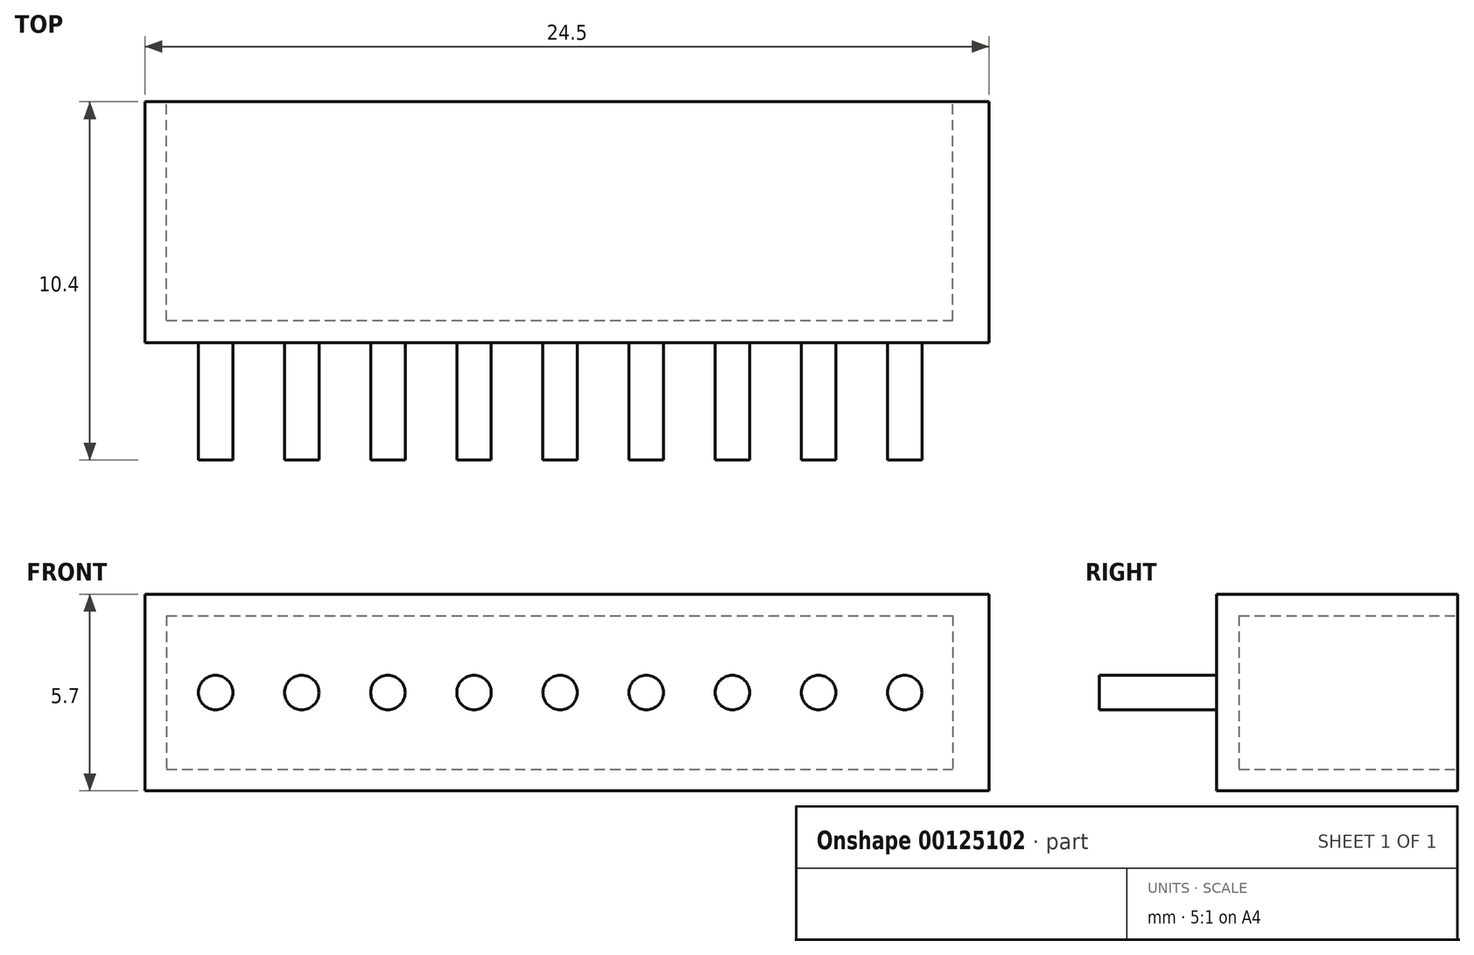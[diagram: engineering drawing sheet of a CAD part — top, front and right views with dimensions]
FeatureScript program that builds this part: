
annotation { "Feature Type Name" : "Feature", "Feature Type Description" : "" }
export const myFeature = defineFeature(function(context is Context, id is Id, definition is map)
    precondition{}
    {
        {
            var Q0;
            Q0=qCreatedBy(makeId("Front.planeOp"),FACE);
            var sketch = newSketch(context, id + "F0", { "sketchPlane" : qUnion([Q0])});
            skLineSegment(sketch, "E0.bottom", {"start": v(12.25, 2.85) * mm, "end": v(-12.25, 2.85) * mm});
            skLineSegment(sketch, "E0.top", {"start": v(12.25, -2.85) * mm, "end": v(-12.25, -2.85) * mm});
            skLineSegment(sketch, "E0.left", {"start": v(12.25, 2.85) * mm, "end": v(12.25, -2.85) * mm});
            skLineSegment(sketch, "E0.right", {"start": v(-12.25, 2.85) * mm, "end": v(-12.25, -2.85) * mm});
            skPoint(sketch, "E0.middle", {"position": v(0, 0) * mm});
            skSolve(sketch);
        }
        {
            var Q0;
            Q0 = qSketchRegion(id + "F0", true);
            extrude(context, id + "F1", {"entities" : qUnion([Q0]), "depth" : 7 * mm});
        }
        {
            var Q0;
            Q0=makeQuery(id+"F1.opExtrude","CAP_FACE",FACE,{"disambiguationData":[OSD([sQuery(id+"F0.wireOp",EDGE,"E0.bottom"),sQuery(id+"F0.wireOp",EDGE,"E0.top"),sQuery(id+"F0.wireOp",EDGE,"E0.left"),sQuery(id+"F0.wireOp",EDGE,"E0.right")])],"isStart":false});
            var sketch = newSketch(context, id + "F2", { "sketchPlane" : qUnion([Q0])});
            skLineSegment(sketch, "E1", {"start": v(0, 0) * mm, "end": v(9.8, 0) * mm, "construction": true});
            skCircle(sketch, "E2", {"center": v(9.8, 0) * mm, "radius": 0.5 * mm});
            skCircle(sketch, "E3.1.0.0", {"center": v(7.3, 0) * mm, "radius": 0.5 * mm});
            skCircle(sketch, "E3.2.0.0", {"center": v(4.8, 0) * mm, "radius": 0.5 * mm});
            skCircle(sketch, "E3.3.0.0", {"center": v(2.3, 0) * mm, "radius": 0.5 * mm});
            skCircle(sketch, "E3.4.0.0", {"center": v(-0.2, 0) * mm, "radius": 0.5 * mm});
            skCircle(sketch, "E3.5.0.0", {"center": v(-2.7, 0) * mm, "radius": 0.5 * mm});
            skCircle(sketch, "E3.6.0.0", {"center": v(-5.2, 0) * mm, "radius": 0.5 * mm});
            skCircle(sketch, "E3.7.0.0", {"center": v(-7.7, 0) * mm, "radius": 0.5 * mm});
            skCircle(sketch, "E3.8.0.0", {"center": v(-10.2, 0) * mm, "radius": 0.5 * mm});
            skLineSegment(sketch, "E3.direction1", {"start": v(9.8, 0) * mm, "end": v(7.3, 0) * mm, "construction": true});
            skLineSegment(sketch, "E4", {"start": v(9.8, 0) * mm, "end": v(12.25, 0) * mm, "construction": true});
            skSolve(sketch);
        }
        {
            var Q0;
            Q0 = qSketchRegion(id + "F2", true);
            extrude(context, id + "F3", {"entities" : qUnion([Q0]), "operationType" : NewBodyOperationType.ADD, "depth" : 3.4 * mm});
        }
        {
            var Q0;
            Q0=makeQuery(id+"F1.opExtrude","CAP_FACE",FACE,{"disambiguationData":[OSD([sQuery(id+"F0.wireOp",EDGE,"E0.bottom"),sQuery(id+"F0.wireOp",EDGE,"E0.top"),sQuery(id+"F0.wireOp",EDGE,"E0.left"),sQuery(id+"F0.wireOp",EDGE,"E0.right")])],"isStart":true});
            var sketch = newSketch(context, id + "F4", { "sketchPlane" : qUnion([Q0])});
            skLineSegment(sketch, "E5.bottom", {"start": v(11.63, 2.23) * mm, "end": v(-11.2, 2.23) * mm});
            skLineSegment(sketch, "E5.top", {"start": v(11.63, -2.23) * mm, "end": v(-11.2, -2.23) * mm});
            skLineSegment(sketch, "E5.left", {"start": v(11.63, 2.23) * mm, "end": v(11.63, -2.23) * mm});
            skLineSegment(sketch, "E5.right", {"start": v(-11.2, 2.23) * mm, "end": v(-11.2, -2.23) * mm});
            skPoint(sketch, "E5.middle", {"position": v(0.21, 0) * mm});
            skSolve(sketch);
        }
        {
            var Q0;
            Q0 = qSketchRegion(id + "F4", true);
            extrude(context, id + "F5", {"entities" : qUnion([Q0]), "operationType" : NewBodyOperationType.REMOVE, "oppositeDirection" : true, "depth" : 6.35 * mm});
        }
    });
